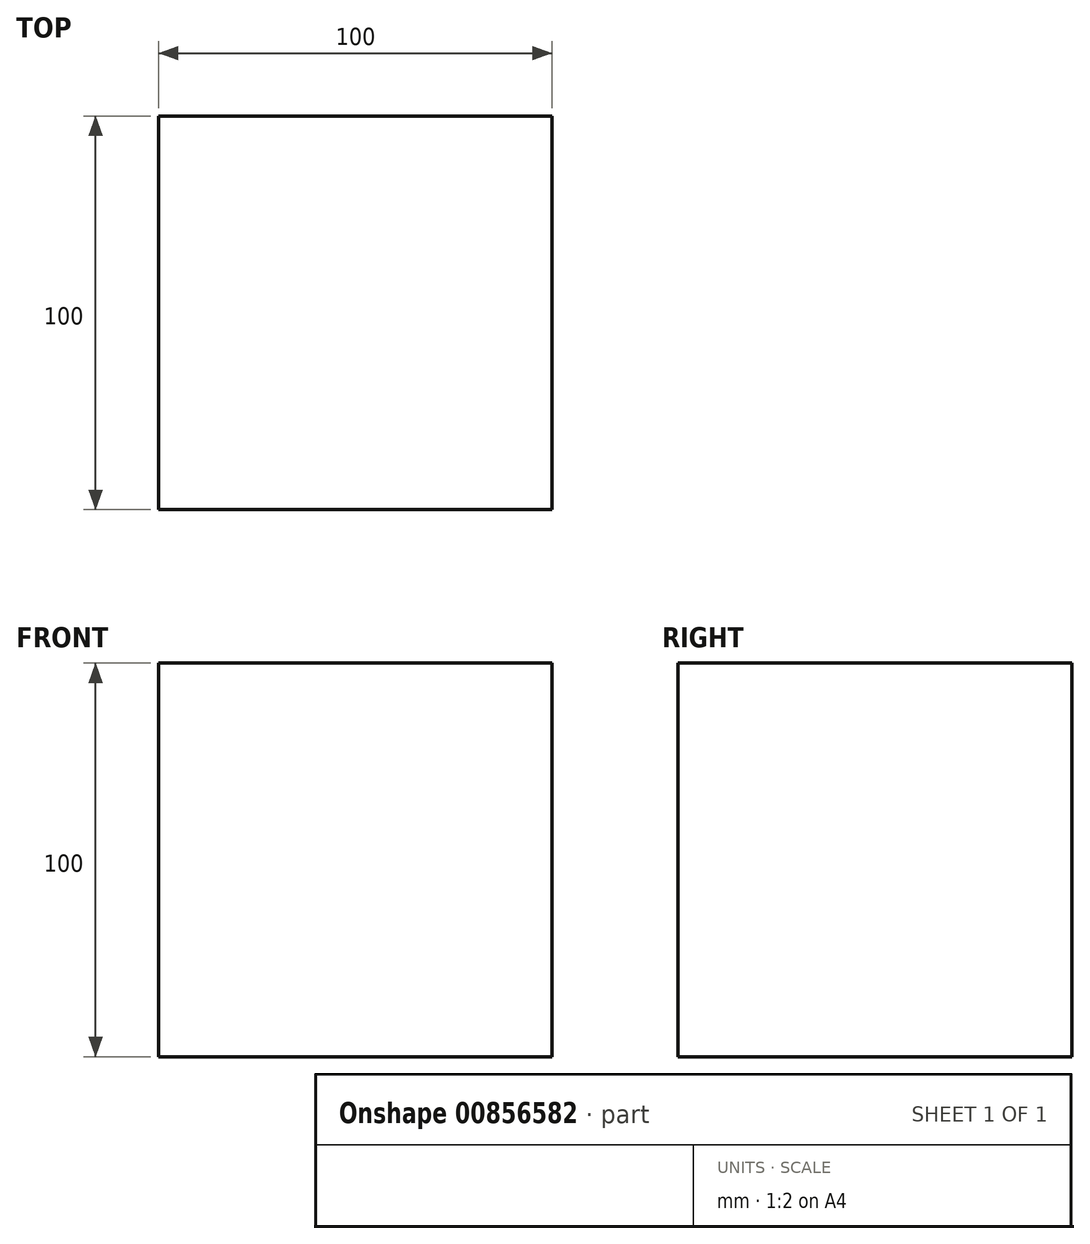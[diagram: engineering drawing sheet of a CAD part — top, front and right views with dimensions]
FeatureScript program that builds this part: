
annotation { "Feature Type Name" : "Feature", "Feature Type Description" : "" }
export const myFeature = defineFeature(function(context is Context, id is Id, definition is map)
    precondition{}
    {
        {
            var Q0;
            Q0=qCreatedBy(makeId("Top.planeOp"),FACE);
            var sketch = newSketch(context, id + "F0", { "sketchPlane" : qUnion([Q0])});
            skLineSegment(sketch, "E0.bottom", {"start": v(-50, 50) * mm, "end": v(50, 50) * mm});
            skLineSegment(sketch, "E0.top", {"start": v(-50, -50) * mm, "end": v(50, -50) * mm});
            skLineSegment(sketch, "E0.left", {"start": v(-50, 50) * mm, "end": v(-50, -50) * mm});
            skLineSegment(sketch, "E0.right", {"start": v(50, 50) * mm, "end": v(50, -50) * mm});
            skSolve(sketch);
        }
        {
            var Q0;
            Q0=makeQuery(id+"F0.imprint","IMPRINT",FACE,{"disambiguationData":[TD([[makeQuery(id+"F0.imprint","IMPRINT",EDGE,{"derivedFrom":sQuery(id+"F0.wireOp",EDGE,"E0.bottom")}),-1.0]])]});
            extrude(context, id + "F1", {"entities" : qUnion([Q0]), "endBound" : BoundingType.SYMMETRIC, "depth" : 100 * mm, "offsetDistance" : 25 * mm});
        }
    });
